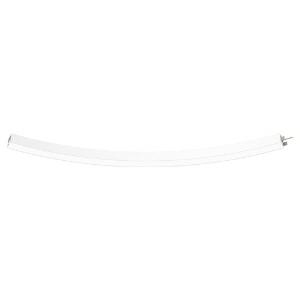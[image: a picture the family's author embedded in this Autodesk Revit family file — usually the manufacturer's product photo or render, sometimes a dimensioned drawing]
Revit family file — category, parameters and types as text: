
# Revit family: super-g_slim_super_g_slim_5200_45deg_ab_ps_led__42w_5530lm_3000k_cri_80_350-1460_6ecf
name_source: partatom
category: Leuchten
revit_build: Autodesk Revit 2016 (Build: 20190508_0715(x64)
units: mm (PartAtom-declared; Revit-internal decimal feet)

## family parameters
Basisbauteil = Fläche
Beim Laden mit Abzugskörper schneiden = Nein
Bemaßung runder Anschluss = Durchmesser verwenden
Gemeinsam genutzt = Nein
Lichtquelle = Nein
Raumberechnungspunkt = Nein
Teiletyp = Normal

## types (1)
- 350-1460-D01 (1 x LED, 480 lm, 3000K)
    Approval mark = CE
    Beschreibung = The insert consists of aluminum-extruded profile. Charming SOFT-EDGE design ensure unparalleled styling. The ballast is integrated and allows for an operation with 220-240V (50/60Hz). SUPER-G SLIM (# 350-1460) ist not dimmable (on/off).
    CIE Flux Codes = 48 79 96 100 71
    Color Rendering = 1B/80…89
    Color Temperature = 3000K
    Height = 90 mm
    Hersteller = Prolicht
    Lamp Light Flux = 480 lm
    Lamp count = 1
    Lampe = 1 x LED
    Length = 146 mm
    Luminous efficacy = 103 lm/W
    ModVariant = Nein
    Modell = 350-1460
    Mounting Place = Ceiling
    Mounting Type = Surface mounted
    Number of Poles = 1
    OnlyDefault = Ja
    Power Factor = 1
    Product Name = SUPER-G SLIM__SUPER G SLIM 5200/45° AB PS LED: 42W 5530lm 3000K CRI:80
    Product group = Surface profile systems
    ProductGroupID = 335
    Protection Class = Protection class I
    Protection Degree = IP 20
    RLX_Detail_Level = 1
    RlxData = <blob elided: 31653 chars, md5=bf3efa21>
    Scheinlast = 46 VA
    Socket = socket
    Standby Power = 0 W
    System Light Flux = 4765 lm
    System Power = 46 W
    Typenbild = 350-1460.jpg
    URL = http://relux.com
    VarID = 350-1460-d01
    Voltage = 0 V
    Vorgabe-Ansicht = 1800 mm
    Weight = 0.00 kg
    Width = 65 mm

## geometry (parser evidence)
native form markers: Blend x4, Sweep x42
no freeform markers — native parametric forms only
